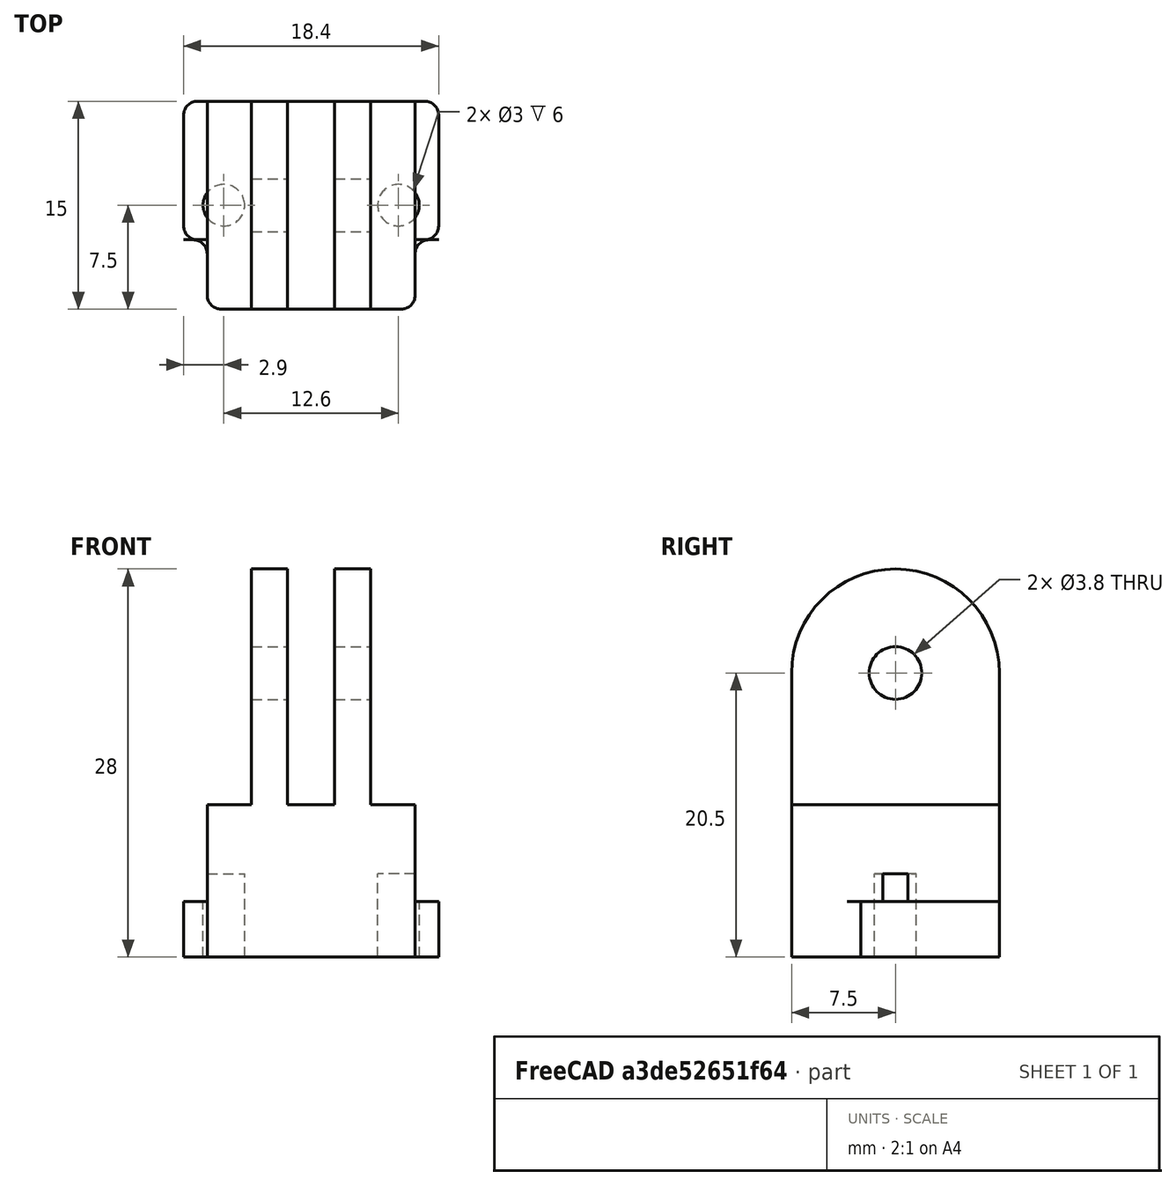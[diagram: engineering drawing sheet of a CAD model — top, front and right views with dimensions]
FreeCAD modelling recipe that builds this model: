
FCSTD DOCUMENT  (FreeCAD 0.19R23578 (Git))
Label: hmc5883l
License: FreeArt
LicenseURL: http://artlibre.org/licence/lal
objects: Part::Box×2, Spreadsheet::Sheet×1, Part::Cylinder×1, Part::FeaturePython×1, Part::Feature×1, Part::MultiFuse×1, Part::Cut×1, Part::Fillet×1, App::Part×1
note: 8 computed .brp shape members not serialized (recipe doc carries the construction recipe); baked Part::Feature solids carry a one-line shape summary decoded from their .brp

FEATURE [Spreadsheet::Sheet] Spreadsheet  label="p"
  cells = A1=pcb_x; B1(pcb_x)==18.4mm; A2=pcb_y; B2(pcb_y)==10mm; A3=pcb_z; B3(pcb_z)==1.7mm; A4=hole_dist_x; B4(hole_dist_x)==12.6mm; A5=hole_offset_y; B5(hole_offset_y)==2.5mm; A6=hole_r; B6(hole_r)==1.5mm; A7=stick_width; B7(stick_width)==15mm; A8=stick_length; B8(stick_length)==10mm; A9=pcb_wall; B9(pcb_wall)==4mm; A10=pcb_back; B10(pcb_back)==2mm
FEATURE [Part::Cylinder] Cylinder  label="bolt hole"
  Angle = 360
  AttacherType = Attacher::AttachEngine3D
  Height = 10
  Radius = 1.5
  expr: Radius = <<p>>.hole_r
FEATURE [Part::FeaturePython] Array  label="bolt hole array"  # Draft array (typed FeaturePython)
  Angle = 360
  ArrayType = 0
  Axis = (0,0,1)
  Base = -> Cylinder
  Center = (0,0,0)
  Fuse = false
  IntervalAxis = (0,0,0)
  IntervalX = (12.6,0,0)
  IntervalY = (0,1,0)
  IntervalZ = (0,0,1)
  NumberPolar = 1
  NumberX = 2
  NumberY = 1
  NumberZ = 1
  Placement = pos=(1.2,7.5,-2) rot=(0,0,1;0rad)
  expr: .Placement.Base.x = (<<p>>.stick_width - <<p>>.hole_dist_x) / 2
  expr: .IntervalX.x = <<p>>.hole_dist_x
  expr: .Placement.Base.y = <<p>>.stick_width - <<p>>.pcb_y + <<p>>.hole_offset_y
FEATURE [Part::Box] Box002  label="stick cube"
  AttacherType = Attacher::AttachEngine3D
  Height = 10
  Length = 15
  Placement = pos=(0,0,2) rot=(0,0,1;0rad)
  Width = 15
  expr: Length = <<p>>.stick_width
  expr: Width = <<p>>.stick_width
  expr: .Placement.Base.z = <<p>>.pcb_back
  expr: Height = <<p>>.stick_length
FEATURE [Part::Feature] Cut001001  label="side 2 cut001"
  Placement = pos=(7.5,7.5,10) rot=(0,0,1;1.5708rad)
  shape: bbox 15 x 15 x 20 mm, 16 faces (baked)
  expr: .Placement.Base.y = <<p>>.stick_width / 2
  expr: .Placement.Base.x = <<p>>.stick_width / 2
  expr: .Placement.Base.z = <<p>>.stick_length
FEATURE [Part::Box] Box003  label="pcb wall"
  AttacherType = Attacher::AttachEngine3D
  Height = 4
  Length = 18.4
  Placement = pos=(-1.7,5,2) rot=(0,0,1;0rad)
  Width = 10
  expr: .Placement.Base.z = <<p>>.pcb_wall / 2
  expr: .Placement.Base.x = -(<<p>>.pcb_x - <<p>>.stick_width) / 2
  expr: Length = <<p>>.pcb_x
  expr: Width = <<p>>.pcb_y
  expr: Height = <<p>>.pcb_wall
  expr: .Placement.Base.y = <<p>>.stick_width - <<p>>.pcb_y
FEATURE [Part::MultiFuse] Fusion  label="holder fusion"
  Shapes = -> [Box002,Cut001001,Box003]
FEATURE [Part::Cut] Cut  label="sensor cut"
  Base = -> Fusion
  Tool = -> Array
FEATURE [Part::Fillet] Fillet  label="sensor fillet"
  Base = -> Cut
  Edges = 8 edges r=1: [Edge1,Edge9,Edge11,Edge31,Edge40,Edge52,Edge70,Edge93]
FEATURE [App::Part] Part  label="hmc5883l sensor part"
  Group = -> [Fillet]
  Origin = -> Origin
